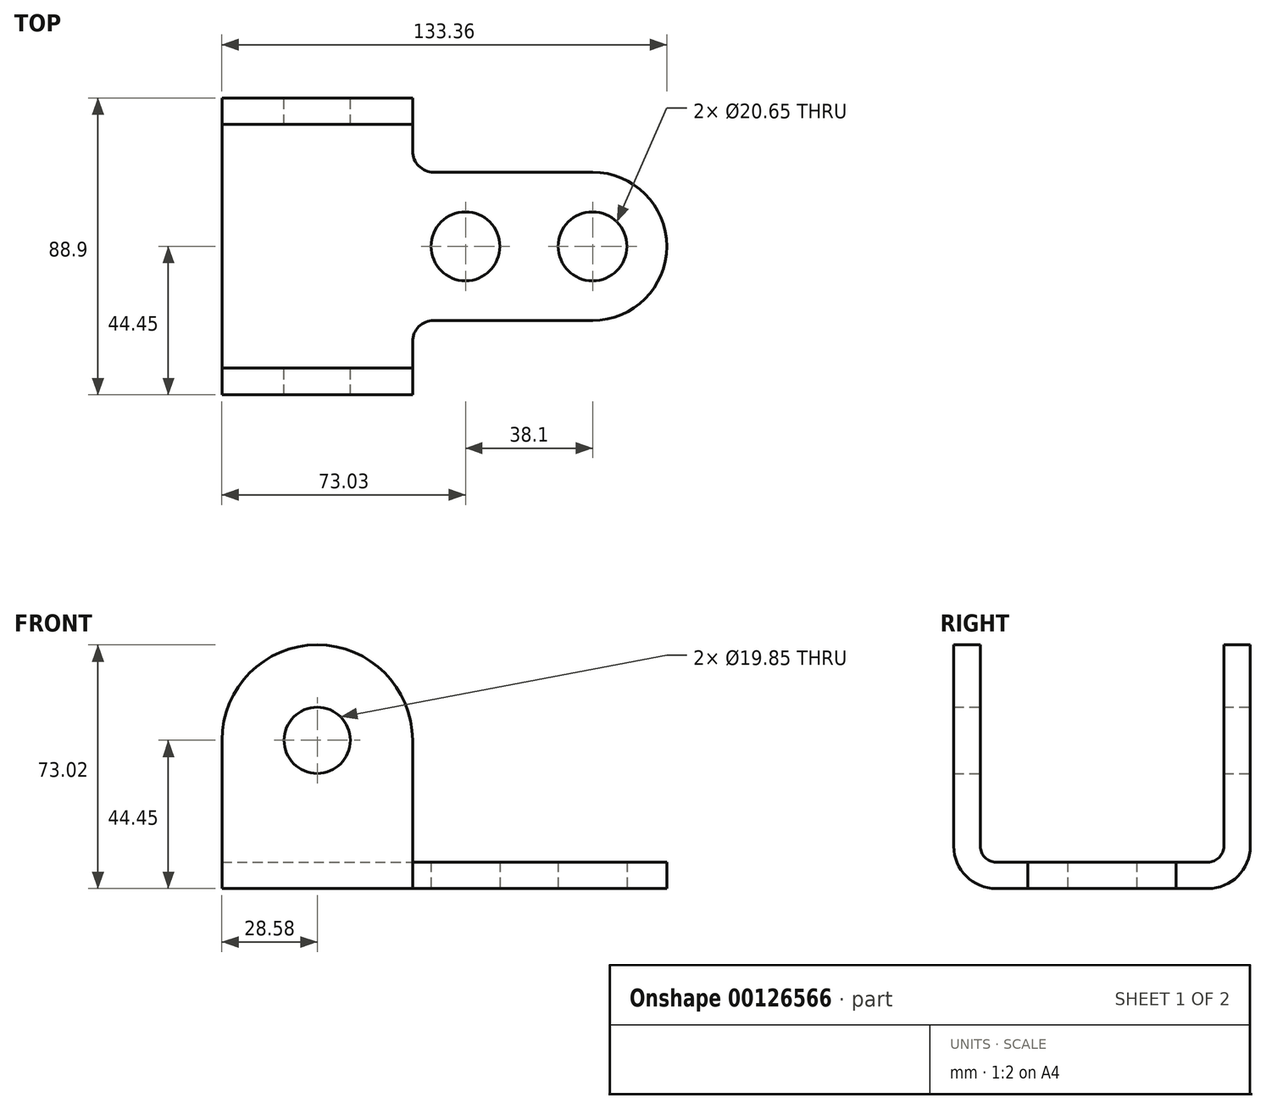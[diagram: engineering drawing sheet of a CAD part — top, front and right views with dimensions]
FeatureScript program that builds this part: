
annotation { "Feature Type Name" : "Feature", "Feature Type Description" : "" }
export const myFeature = defineFeature(function(context is Context, id is Id, definition is map)
    precondition{}
    {
        {
            var Q0;
            Q0=qCreatedBy(makeId("Front.planeOp"),FACE);
            var sketch = newSketch(context, id + "F0", { "sketchPlane" : qUnion([Q0])});
            skCircle(sketch, "E0", {"center": v(0, 0) * mm, "radius": 9.92 * mm});
            skArc(sketch, "E1", {"start": v(-28.58, 0) * mm, "mid": v(0, 28.58) * mm, "end": v(28.58, 0) * mm});
            skLineSegment(sketch, "E2", {"start": v(-28.58, 0) * mm, "end": v(-28.58, -44.45) * mm});
            skLineSegment(sketch, "E3.MirrorCS", {"start": v(28.58, 0) * mm, "end": v(28.58, -44.45) * mm});
            skLineSegment(sketch, "E4", {"start": v(-28.58, -44.45) * mm, "end": v(28.58, -44.45) * mm});
            skLineSegment(sketch, "E5", {"start": v(28.58, -44.45) * mm, "end": v(104.78, -44.45) * mm});
            skLineSegment(sketch, "E6", {"start": v(104.78, -44.45) * mm, "end": v(104.78, -36.51) * mm});
            skLineSegment(sketch, "E7", {"start": v(104.78, -36.51) * mm, "end": v(28.58, -36.51) * mm});
            skSolve(sketch);
        }
        {
            var Q0;
            Q0 = qSketchRegion(id + "F0", true);
            extrude(context, id + "F1", {"entities" : qUnion([Q0]), "endBound" : BoundingType.SYMMETRIC, "depth" : 88.9 * mm});
        }
        {
            var Q0;
            Q0=makeQuery(id+"F1.opExtrude","SWEPT_FACE",FACE,{"disambiguationData":[OSD([sQuery(id+"F0.wireOp",EDGE,"E1")])]});
            var Q1;
            Q1=makeQuery(id+"F1.opExtrude","SWEPT_FACE",FACE,{"disambiguationData":[OSD([sQuery(id+"F0.wireOp",EDGE,"E0")])]});
            var Q2;
            Q2=makeQuery(id+"F1.opExtrude","SWEPT_FACE",FACE,{"disambiguationData":[OSD([sQuery(id+"F0.wireOp",EDGE,"E3.MirrorCS")])]});
            var Q3;
            Q3=makeQuery(id+"F1.opExtrude","SWEPT_FACE",FACE,{"disambiguationData":[OSD([sQuery(id+"F0.wireOp",EDGE,"E2")])]});
            shell(context, id + "F2", {"entities" : qUnion([Q0, Q1, Q2, Q3]), "thickness" : 7.94 * mm});
        }
        {
            var Q0;
            Q0=makeQuery(id+"F2.opShell","MERGE",FACE,{"derivedFrom":[makeQuery(id+"F1.opExtrude","SWEPT_FACE",FACE,{"disambiguationData":[OSD([sQuery(id+"F0.wireOp",EDGE,"E4"),sQuery(id+"F0.wireOp",EDGE,"E5")])]}),makeQuery(id+"F1.opExtrude","SWEPT_FACE",FACE,{"disambiguationData":[OSD([sQuery(id+"F0.wireOp",EDGE,"E7")])]})]});
            var sketch = newSketch(context, id + "F3", { "sketchPlane" : qUnion([Q0])});
            skCircle(sketch, "E8", {"center": v(82.55, 0) * mm, "radius": 10.33 * mm});
            skCircle(sketch, "E9", {"center": v(44.45, 0) * mm, "radius": 10.33 * mm});
            skArc(sketch, "E10", {"start": v(82.55, 22.22) * mm, "mid": v(104.77, 0) * mm, "end": v(82.55, -22.23) * mm});
            skLineSegment(sketch, "E11", {"start": v(82.55, -22.23) * mm, "end": v(28.57, -22.23) * mm});
            skLineSegment(sketch, "E12", {"start": v(28.57, -22.23) * mm, "end": v(28.57, -44.45) * mm});
            skLineSegment(sketch, "E13", {"start": v(82.55, 22.22) * mm, "end": v(28.57, 22.22) * mm});
            skLineSegment(sketch, "E14", {"start": v(28.57, 22.22) * mm, "end": v(28.57, 44.45) * mm});
            skSolve(sketch);
        }
        {
            var Q0;
            Q0=makeQuery(id+"F3.imprint","IMPRINT",FACE,{"disambiguationData":[TD([[makeQuery(id+"F3.imprint","IMPRINT",EDGE,{"derivedFrom":sQuery(id+"F3.wireOp",EDGE,"E9")}),1.0]])]});
            var Q1;
            Q1=makeQuery(id+"F3.imprint","IMPRINT",FACE,{"disambiguationData":[TD([[makeQuery(id+"F3.imprint","IMPRINT",EDGE,{"derivedFrom":sQuery(id+"F3.wireOp",EDGE,"E8")}),1.0]])]});
            var Q2;
            {var subQ4=sQuery(id+"F3.wireOp",EDGE,"E11");Q2=makeQuery(id+"F3.imprint","IMPRINT",FACE,{"disambiguationData":[TD([[makeQuery(id+"F3.imprint","IMPRINT",EDGE,{"derivedFrom":subQ4}),1.0]])]});}
            var Q3;
            {var subQ6=sQuery(id+"F3.wireOp",EDGE,"E13");Q3=makeQuery(id+"F3.imprint","IMPRINT",FACE,{"disambiguationData":[TD([[makeQuery(id+"F3.imprint","IMPRINT",EDGE,{"derivedFrom":subQ6}),-1.0]])]});}
            extrude(context, id + "F4", {"entities" : qUnion([Q0, Q1, Q2, Q3]), "operationType" : NewBodyOperationType.REMOVE, "endBound" : BoundingType.THROUGH_ALL, "oppositeDirection" : true, "depth" : 25.4 * mm});
        }
        {
            var Q0;
            Q0=makeQuery(id+"F4.boolean.opBoolean","COPY",EDGE,{"derivedFrom":makeQuery(id+"F4.opExtrude","SWEPT_EDGE",EDGE,{"disambiguationData":[OSD([sQuery(id+"F3.wireOp",EDGE,"E11"),sQuery(id+"F3.wireOp",EDGE,"E12")])]})});
            var Q1;
            Q1=makeQuery(id+"F4.boolean.opBoolean","COPY",EDGE,{"derivedFrom":makeQuery(id+"F4.opExtrude","SWEPT_EDGE",EDGE,{"disambiguationData":[OSD([sQuery(id+"F3.wireOp",EDGE,"E13"),sQuery(id+"F3.wireOp",EDGE,"E14")])]})});
            fillet(context, id + "F5", {"entities" : qUnion([Q0, Q1]), "radius" : 6.35 * mm, "tangentPropagation" : true, "allowEdgeOverflow" : false});
        }
        {
            var Q0;
            {var subQ0=sQuery(id+"F0.wireOp",EDGE,"E5");var subQ1=sQuery(id+"F0.wireOp",EDGE,"E4");Q0=makeQuery(id+"F2.opShell","OFFSET_EDGE",EDGE,{"disambiguationData":[OSD([subQ1,subQ0]),TDD([makeQuery(id+"F1.opExtrude","CAP_EDGE",EDGE,{"disambiguationData":[OSD([subQ1,subQ0])],"isStart":false})])]});}
            var Q1;
            {var subQ0=sQuery(id+"F0.wireOp",EDGE,"E5");var subQ1=sQuery(id+"F0.wireOp",EDGE,"E4");Q1=makeQuery(id+"F2.opShell","OFFSET_EDGE",EDGE,{"disambiguationData":[OSD([subQ1,subQ0]),TDD([makeQuery(id+"F1.opExtrude","CAP_EDGE",EDGE,{"disambiguationData":[OSD([subQ1,subQ0])],"isStart":true})])]});}
            fillet(context, id + "F6", {"entities" : qUnion([Q0, Q1]), "radius" : 4.76 * mm, "tangentPropagation" : true, "allowEdgeOverflow" : false});
        }
        {
            var Q0;
            Q0=makeQuery(id+"F1.opExtrude","CAP_EDGE",EDGE,{"disambiguationData":[OSD([sQuery(id+"F0.wireOp",EDGE,"E4"),sQuery(id+"F0.wireOp",EDGE,"E5")])],"isStart":false});
            var Q1;
            Q1=makeQuery(id+"F1.opExtrude","CAP_EDGE",EDGE,{"disambiguationData":[OSD([sQuery(id+"F0.wireOp",EDGE,"E4"),sQuery(id+"F0.wireOp",EDGE,"E5")])],"isStart":true});
            fillet(context, id + "F7", {"entities" : qUnion([Q0, Q1]), "radius" : 12.7 * mm, "tangentPropagation" : true, "allowEdgeOverflow" : false});
        }
    });
